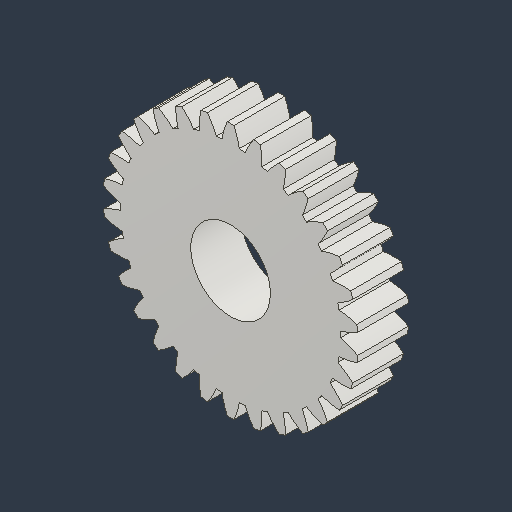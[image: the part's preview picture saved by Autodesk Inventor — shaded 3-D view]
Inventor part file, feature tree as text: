
AUTODESK INVENTOR PART (.ipt)
format: ipt  version: 2024.3 (Build 283343000, 343)  size: 247,296 bytes
history: native  units: mm (DEFAULTED — no unit token found)
features: plane x3, other x3, sketch x2, extrude x1, hole x1
ambient origin geometry x8: Origin, YZ Plane, XZ Plane, XY Plane, X Axis, Y Axis, Z Axis, Center Point
bodies: Solid1 (feature_tree)
feature tree (10):
  extrude  "Extrusion1"  Depth=7.9375mm TaperAngle=0.0deg
  plane  "Work Plane1"
  plane  "Work Plane2"
  plane  "Work Plane3"
  other  "Spur Gear"
  hole  "Hole1"  [1 undecoded]
  sketch  "Sketch1"  dims[d0=39.819801mm d1=7.9375mm d2=0.0mm]
  other  "Srf1"
  sketch  "Sketch3"  dims[d3=37.5mm d4=76.2mm d5=0.0mm d6=0.0mm d7=1.047198mm d9=0.0mm d14=0.0mm d15=101.219mm d16=0.0mm d17=0.0mm d18=0.0mm d19=101.219mm d20=12.446mm d21=19.05mm d22=9.525mm d23=6.35mm d24=14.3117mm d25=25.4mm d26=20.594885mm]
  other  "Pitch Diameter"
note: 1 required parameter value undecoded (feature->parameter linkage not recoverable at this tier; creation-order binding heuristic only, values carry confidence <= 0.55)
